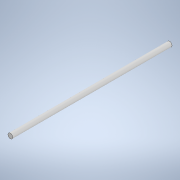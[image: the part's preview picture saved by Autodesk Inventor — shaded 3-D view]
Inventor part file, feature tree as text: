
AUTODESK INVENTOR PART (.ipt)
format: ipt  version: 2021 (Build 250183000, 183)  size: 91,136 bytes
history: native  units: mm
features: extrude x1, sketch x1
ambient origin geometry x8: Origin, YZ Plane, XZ Plane, XY Plane, X Axis, Y Axis, Z Axis, Center Point
bodies: Solid1 (feature_tree)
feature tree (2):
  extrude  "Extrusion1"  Depth=100.0mm TaperAngle=0.0deg
  sketch  "Sketch1"  dims[d0=3.0mm d1=100.0mm d2=0.0mm]
